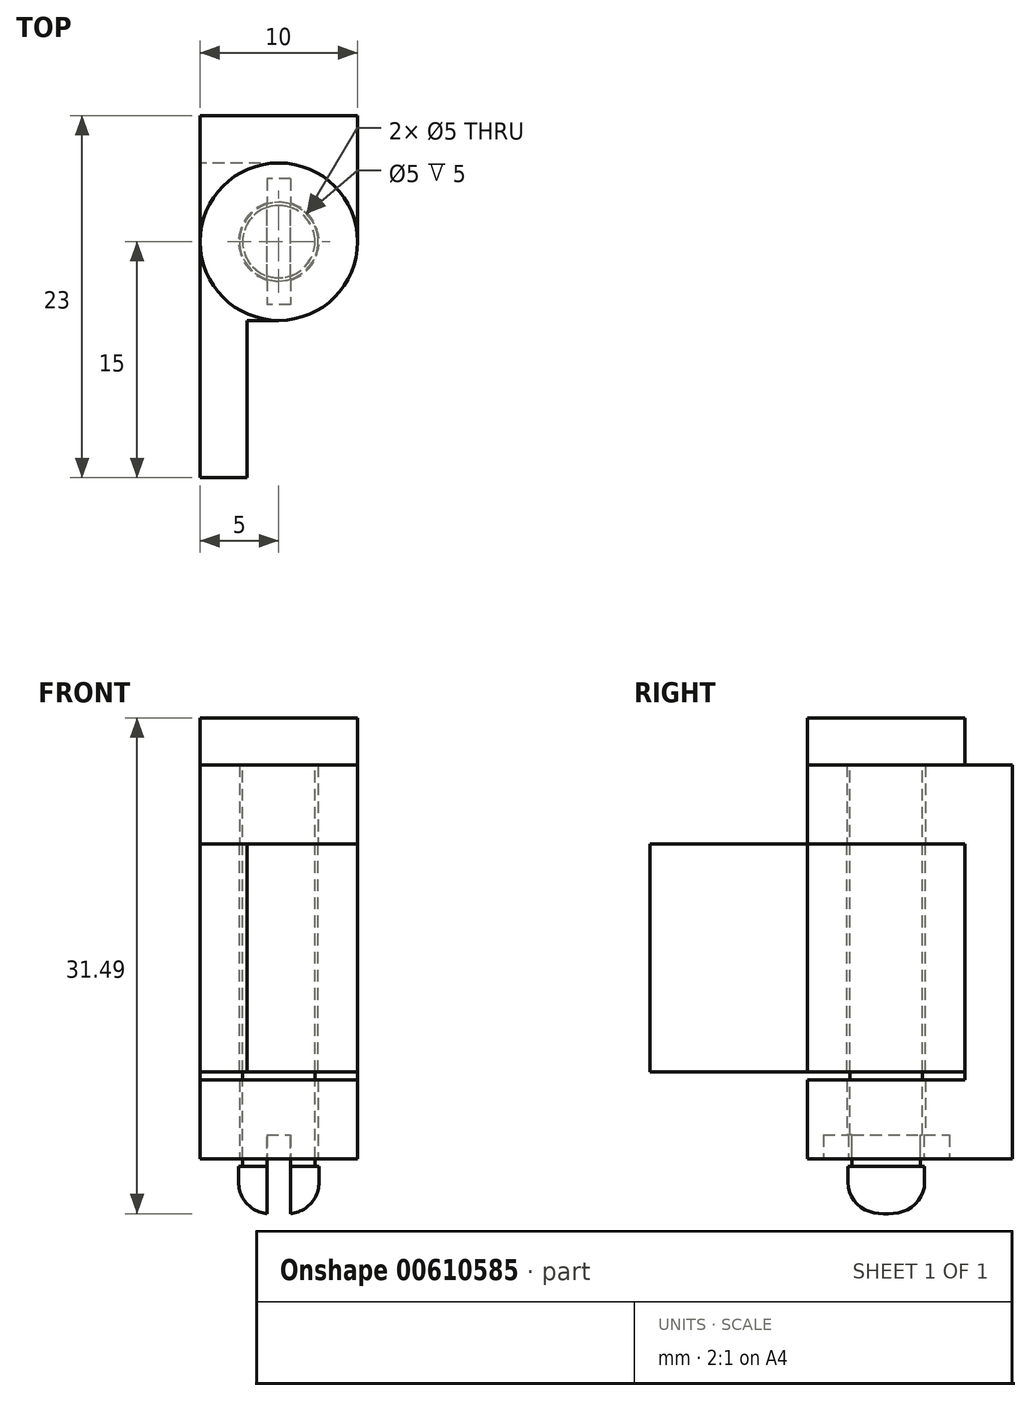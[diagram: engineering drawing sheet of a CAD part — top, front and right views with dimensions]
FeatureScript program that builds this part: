
annotation { "Feature Type Name" : "Feature", "Feature Type Description" : "" }
export const myFeature = defineFeature(function(context is Context, id is Id, definition is map)
    precondition{}
    {
        {
            var Q0;
            Q0=qCreatedBy(makeId("Front.planeOp"),FACE);
            var sketch = newSketch(context, id + "F0", { "sketchPlane" : qUnion([Q0])});
            skLineSegment(sketch, "E0.bottom", {"start": v(0, 25) * mm, "end": v(10, 25) * mm});
            skLineSegment(sketch, "E0.top", {"start": v(0, 0) * mm, "end": v(10, 0) * mm});
            skLineSegment(sketch, "E0.left", {"start": v(0, 25) * mm, "end": v(0, 0) * mm});
            skLineSegment(sketch, "E0.right", {"start": v(10, 25) * mm, "end": v(10, 0) * mm});
            skArc(sketch, "E1", {"start": v(0, 25) * mm, "mid": v(-9.43, 12.5) * mm, "end": v(0, 0) * mm});
            skArc(sketch, "E2", {"start": v(10, 0) * mm, "mid": v(19.43, 12.5) * mm, "end": v(10, 25) * mm});
            skSolve(sketch);
        }
        {
            var Q0;
            Q0=makeQuery(id+"F0.imprint","IMPRINT",FACE,{"disambiguationData":[TD([[makeQuery(id+"F0.imprint","IMPRINT",EDGE,{"derivedFrom":sQuery(id+"F0.wireOp",EDGE,"E0.bottom")}),-1.0]])]});
            extrude(context, id + "F1", {"entities" : qUnion([Q0]), "depth" : 3 * mm, "offsetDistance" : 25 * mm});
        }
        {
            var Q0;
            Q0=makeQuery(id+"F1.opExtrude","SWEPT_FACE",FACE,{"disambiguationData":[OSD([sQuery(id+"F0.wireOp",EDGE,"E0.top")])]});
            var sketch = newSketch(context, id + "F2", { "sketchPlane" : qUnion([Q0])});
            skCircle(sketch, "E3", {"center": v(5, 8) * mm, "radius": 5 * mm});
            skLineSegment(sketch, "E4", {"start": v(10, 3) * mm, "end": v(10, 8) * mm});
            skLineSegment(sketch, "E5", {"start": v(0, 3) * mm, "end": v(0, 8) * mm});
            skCircle(sketch, "E6", {"center": v(5, 8) * mm, "radius": 2.5 * mm});
            skSolve(sketch);
        }
        {
            var Q0;
            Q0=makeQuery(id+"F2.imprint","IMPRINT",FACE,{"disambiguationData":[TD([[makeQuery(id+"F2.imprint","IMPRINT",EDGE,{"derivedFrom":sQuery(id+"F2.wireOp",EDGE,"E6")}),-1.0]])]});
            var Q1;
            {var subQ0=sQuery(id+"F2.wireOp",EDGE,"E5");Q1=makeQuery(id+"F2.imprint","IMPRINT",FACE,{"disambiguationData":[TD([[makeQuery(id+"F2.imprint","IMPRINT",EDGE,{"derivedFrom":subQ0}),-1.0]])]});}
            var Q2;
            {var subQ0=sQuery(id+"F2.wireOp",EDGE,"E4");Q2=makeQuery(id+"F2.imprint","IMPRINT",FACE,{"disambiguationData":[TD([[makeQuery(id+"F2.imprint","IMPRINT",EDGE,{"derivedFrom":subQ0}),1.0]])]});}
            extrude(context, id + "F3", {"entities" : qUnion([Q0, Q1, Q2]), "operationType" : NewBodyOperationType.ADD, "oppositeDirection" : true, "depth" : 5 * mm, "offsetDistance" : 25 * mm});
        }
        {
            var Q0;
            {var subQ0=sQuery(id+"F0.wireOp",EDGE,"E0.top");Q0=makeQuery(id+"F3.boolean.opBoolean","MERGE",FACE,{"derivedFrom":[makeQuery(id+"F1.opExtrude","SWEPT_FACE",FACE,{"disambiguationData":[OSD([subQ0])]}),makeQuery(id+"F3.opExtrude","CAP_FACE",FACE,{"disambiguationData":[OSD([subQ0,sQuery(id+"F2.wireOp",EDGE,"E3"),sQuery(id+"F2.wireOp",EDGE,"E4"),sQuery(id+"F2.wireOp",EDGE,"E5"),sQuery(id+"F2.wireOp",EDGE,"E6")])],"isStart":true})]});}
            extrude(context, id + "F4", {"entities" : qUnion([Q0]), "operationType" : NewBodyOperationType.ADD, "oppositeDirection" : true, "depth" : 25 * mm, "offsetDistance" : 25 * mm, "hasSecondDirection" : true, "secondDirectionOppositeDirection" : true, "secondDirectionDepth" : 20 * mm});
        }
        {
            var Q0;
            Q0=makeQuery(id+"F4.opExtrude","CAP_FACE",FACE,{"disambiguationData":[OSD([sQuery(id+"F0.wireOp",EDGE,"E0.top"),sQuery(id+"F2.wireOp",EDGE,"E3"),sQuery(id+"F2.wireOp",EDGE,"E4"),sQuery(id+"F2.wireOp",EDGE,"E5"),sQuery(id+"F2.wireOp",EDGE,"E6")])],"isStart":true});
            var sketch = newSketch(context, id + "F5", { "sketchPlane" : qUnion([Q0])});
            skCircle(sketch, "E7", {"center": v(5, 8) * mm, "radius": 5 * mm});
            skLineSegment(sketch, "E8.bottom", {"start": v(0, 3) * mm, "end": v(3, 3) * mm});
            skLineSegment(sketch, "E8.top", {"start": v(0, 23) * mm, "end": v(3, 23) * mm});
            skLineSegment(sketch, "E8.left", {"start": v(0, 3) * mm, "end": v(0, 23) * mm});
            skLineSegment(sketch, "E8.right", {"start": v(3, 3) * mm, "end": v(3, 23) * mm});
            skLineSegment(sketch, "E9", {"start": v(3, 3) * mm, "end": v(5, 3) * mm});
            skLineSegment(sketch, "E10", {"start": v(5, 13) * mm, "end": v(3, 13) * mm});
            skSolve(sketch);
        }
        {
            var Q0;
            {var subQ6=sQuery(id+"F5.wireOp",EDGE,"E8.top");Q0=makeQuery(id+"F5.imprint","IMPRINT",FACE,{"disambiguationData":[TD([[makeQuery(id+"F5.imprint","IMPRINT",EDGE,{"derivedFrom":subQ6}),-1.0]])]});}
            var Q1;
            {var subQ1=sQuery(id+"F5.wireOp",EDGE,"E7");var subQ7=makeQuery(id+"F5.imprint","INTERSECT",VERTEX,{"derivedFrom":[subQ1,sQuery(id+"F5.wireOp",EDGE,"E8.left")]});Q1=makeQuery(id+"F5.imprint","IMPRINT",FACE,{"disambiguationData":[TD([[makeQuery(id+"F5.imprint","IMPRINT",EDGE,{"disambiguationData":[TD([[subQ7,1.0]])],"derivedFrom":subQ1}),1.0]])]});}
            var Q2;
            {var subQ5=sQuery(id+"F5.wireOp",EDGE,"E8.bottom");Q2=makeQuery(id+"F5.imprint","IMPRINT",FACE,{"disambiguationData":[TD([[makeQuery(id+"F5.imprint","IMPRINT",EDGE,{"derivedFrom":subQ5}),-1.0]])]});}
            var Q3;
            {var subQ0=sQuery(id+"F5.wireOp",EDGE,"E7");var subQ8=makeQuery(id+"F5.imprint","INTERSECT",VERTEX,{"derivedFrom":[subQ0,sQuery(id+"F5.wireOp",EDGE,"E10")]});Q3=makeQuery(id+"F5.imprint","IMPRINT",FACE,{"disambiguationData":[TD([[makeQuery(id+"F5.imprint","IMPRINT",EDGE,{"disambiguationData":[TD([[subQ8,-1.0]])],"derivedFrom":subQ0}),1.0]])]});}
            var Q4;
            {var subQ0=sQuery(id+"F5.wireOp",EDGE,"E9");Q4=makeQuery(id+"F5.imprint","IMPRINT",FACE,{"disambiguationData":[TD([[makeQuery(id+"F5.imprint","IMPRINT",EDGE,{"derivedFrom":subQ0}),-1.0]])]});}
            var Q5;
            {var subQ0=sQuery(id+"F5.wireOp",EDGE,"E10");Q5=makeQuery(id+"F5.imprint","IMPRINT",FACE,{"disambiguationData":[TD([[makeQuery(id+"F5.imprint","IMPRINT",EDGE,{"derivedFrom":subQ0}),1.0]])]});}
            extrude(context, id + "F6", {"entities" : qUnion([Q0, Q1, Q2, Q3, Q4, Q5]), "depth" : 14.5 * mm, "offsetDistance" : 25 * mm});
        }
        {
            var Q0;
            Q0=makeQuery(id+"F4.boolean.opBoolean","MERGE",FACE,{"derivedFrom":[makeQuery(id+"F1.opExtrude","SWEPT_FACE",FACE,{"disambiguationData":[OSD([sQuery(id+"F0.wireOp",EDGE,"E0.bottom")])]}),makeQuery(id+"F4.opExtrude","CAP_FACE",FACE,{"disambiguationData":[OSD([sQuery(id+"F0.wireOp",EDGE,"E0.top"),sQuery(id+"F2.wireOp",EDGE,"E3"),sQuery(id+"F2.wireOp",EDGE,"E4"),sQuery(id+"F2.wireOp",EDGE,"E5"),sQuery(id+"F2.wireOp",EDGE,"E6")])],"isStart":false})]});
            var sketch = newSketch(context, id + "F7", { "sketchPlane" : qUnion([Q0])});
            skCircle(sketch, "E11", {"center": v(5, -8) * mm, "radius": 2.3 * mm});
            skCircle(sketch, "E12", {"center": v(5, -8) * mm, "radius": 5 * mm});
            skSolve(sketch);
        }
        {
            var Q0;
            Q0=makeQuery(id+"F7.imprint","IMPRINT",FACE,{"disambiguationData":[TD([[makeQuery(id+"F7.imprint","IMPRINT",EDGE,{"derivedFrom":sQuery(id+"F7.wireOp",EDGE,"E11")}),-1.0]])]});
            var Q1;
            Q1=makeQuery(id+"F7.imprint","IMPRINT",FACE,{"disambiguationData":[TD([[makeQuery(id+"F7.imprint","IMPRINT",EDGE,{"derivedFrom":sQuery(id+"F7.wireOp",EDGE,"E11")}),1.0]])]});
            var Q2;
            {var subQ0=sQuery(id+"F7.wireOp",EDGE,"E12");Q2=makeQuery(id+"F7.imprint","IMPRINT",FACE,{"disambiguationData":[TD([[makeQuery(id+"F7.imprint","IMPRINT",EDGE,{"disambiguationData":[OD(0.0)],"derivedFrom":subQ0}),1.0]])]});}
            extrude(context, id + "F8", {"entities" : qUnion([Q0, Q1, Q2]), "depth" : 3 * mm, "offsetDistance" : 25 * mm});
        }
        {
            var Q0;
            Q0=makeQuery(id+"F7.imprint","IMPRINT",FACE,{"disambiguationData":[TD([[makeQuery(id+"F7.imprint","IMPRINT",EDGE,{"derivedFrom":sQuery(id+"F7.wireOp",EDGE,"E11")}),1.0]])]});
            extrude(context, id + "F9", {"entities" : qUnion([Q0]), "operationType" : NewBodyOperationType.ADD, "oppositeDirection" : true, "depth" : 25.5 * mm, "offsetDistance" : 25 * mm});
        }
        {
            var Q0;
            Q0=makeQuery(id+"F9.opExtrude","CAP_FACE",FACE,{"disambiguationData":[OSD([sQuery(id+"F7.wireOp",EDGE,"E11")])],"isStart":false});
            var sketch = newSketch(context, id + "F10", { "sketchPlane" : qUnion([Q0])});
            skCircle(sketch, "E13", {"center": v(5, 8) * mm, "radius": 2.55 * mm});
            skSolve(sketch);
        }
        {
            var Q0;
            Q0 = qSketchRegion(id + "F10", true);
            extrude(context, id + "F11", {"entities" : qUnion([Q0]), "operationType" : NewBodyOperationType.ADD, "depth" : 3 * mm, "offsetDistance" : 25 * mm});
        }
        {
            var Q0;
            Q0=makeQuery(id+"F11.opExtrude","CAP_EDGE",EDGE,{"disambiguationData":[OSD([sQuery(id+"F10.wireOp",EDGE,"E13")])],"isStart":false});
            fillet(context, id + "F12", {"entities" : qUnion([Q0]), "radius" : 2 * mm, "tangentPropagation" : true, "allowEdgeOverflow" : false});
        }
        {
            var Q0;
            Q0=makeQuery(id+"F11.opExtrude","CAP_FACE",FACE,{"disambiguationData":[OSD([sQuery(id+"F10.wireOp",EDGE,"E13")])],"isStart":false});
            var sketch = newSketch(context, id + "F13", { "sketchPlane" : qUnion([Q0])});
            skLineSegment(sketch, "E14.bottom", {"start": v(4.25, 12) * mm, "end": v(5.75, 12) * mm});
            skLineSegment(sketch, "E14.top", {"start": v(4.25, 4) * mm, "end": v(5.75, 4) * mm});
            skLineSegment(sketch, "E14.left", {"start": v(4.25, 12) * mm, "end": v(4.25, 4) * mm});
            skLineSegment(sketch, "E14.right", {"start": v(5.75, 12) * mm, "end": v(5.75, 4) * mm});
            skLineSegment(sketch, "E15.bottom", {"start": v(4.25, 8) * mm, "end": v(5.75, 8) * mm, "construction": true});
            skLineSegment(sketch, "E15.top", {"start": v(4.25, 8) * mm, "end": v(5.75, 8) * mm, "construction": true});
            skLineSegment(sketch, "E15.left", {"start": v(4.25, 8) * mm, "end": v(4.25, 8) * mm});
            skLineSegment(sketch, "E15.right", {"start": v(5.75, 8) * mm, "end": v(5.75, 8) * mm});
            skPoint(sketch, "E16", {"position": v(5, 8) * mm});
            skSolve(sketch);
        }
        {
            var Q0;
            Q0 = qSketchRegion(id + "F13", true);
            extrude(context, id + "F14", {"entities" : qUnion([Q0]), "operationType" : NewBodyOperationType.REMOVE, "oppositeDirection" : true, "depth" : 5 * mm, "offsetDistance" : 25 * mm});
        }
    });
